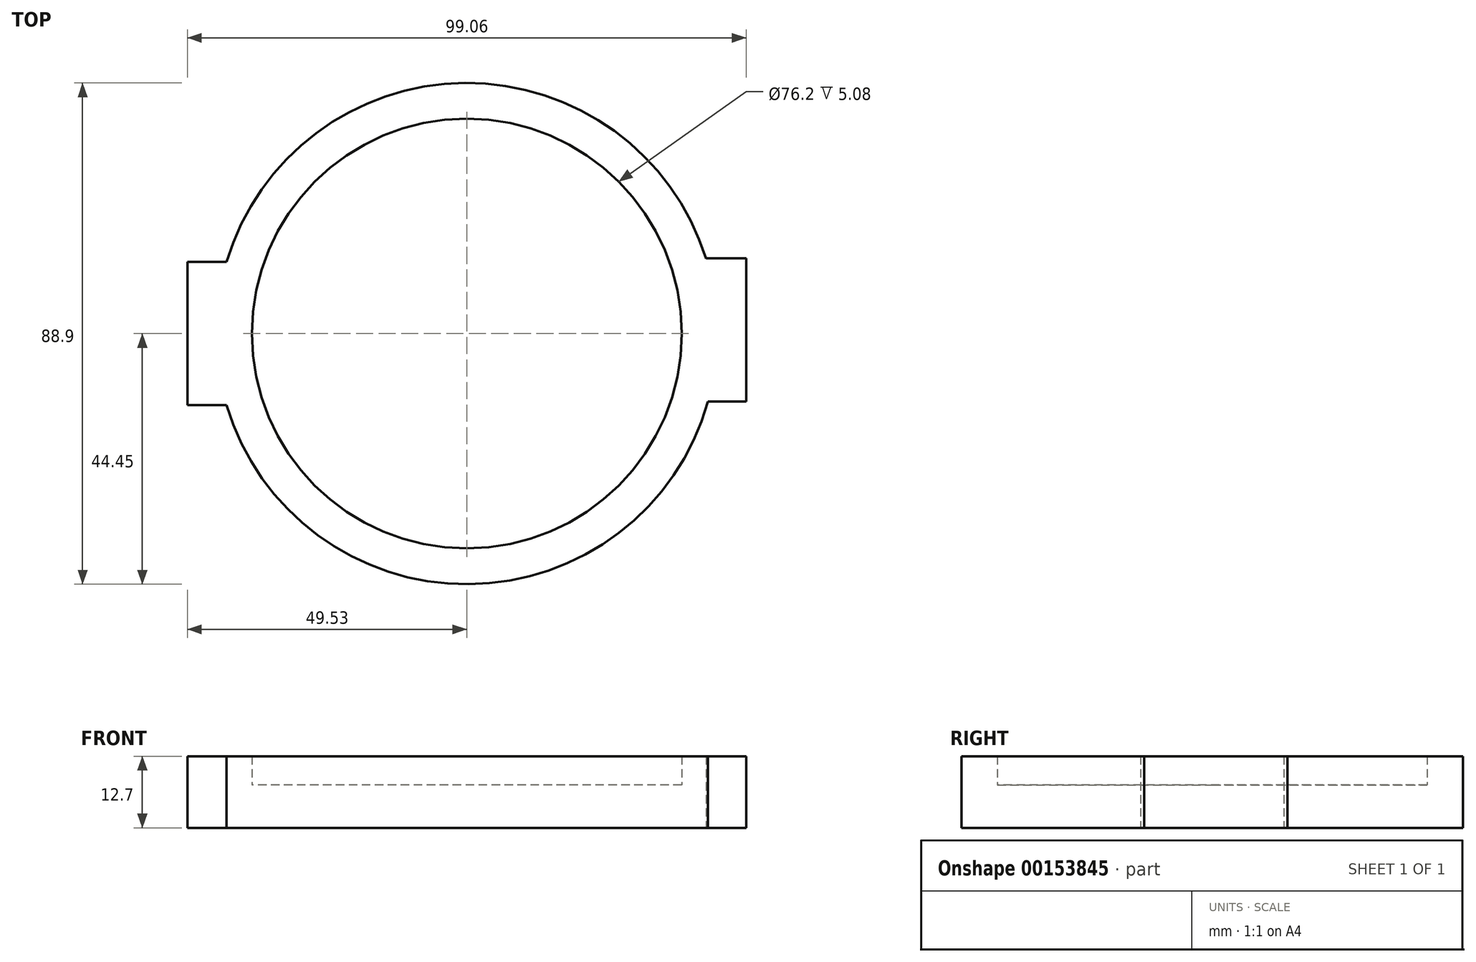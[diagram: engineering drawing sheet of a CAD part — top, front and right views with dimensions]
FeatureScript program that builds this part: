
annotation { "Feature Type Name" : "Feature", "Feature Type Description" : "" }
export const myFeature = defineFeature(function(context is Context, id is Id, definition is map)
    precondition{}
    {
        {
            var Q0;
            Q0=qCreatedBy(makeId("Top.planeOp"),FACE);
            var sketch = newSketch(context, id + "F0", { "sketchPlane" : qUnion([Q0])});
            skArc(sketch, "E0", {"start": v(-42.6, -12.7) * mm, "mid": v(0.32, -44.45) * mm, "end": v(42.78, -12.08) * mm});
            skCircle(sketch, "E1", {"center": v(0, 0) * mm, "radius": 38.1 * mm});
            skLineSegment(sketch, "E2", {"start": v(0, 0) * mm, "end": v(0, 44.45) * mm});
            skLineSegment(sketch, "E3", {"start": v(-49.53, 12.7) * mm, "end": v(-42.6, 12.7) * mm});
            skLineSegment(sketch, "E4", {"start": v(-49.53, -12.7) * mm, "end": v(-42.6, -12.7) * mm});
            skLineSegment(sketch, "E5", {"start": v(49.53, 13.32) * mm, "end": v(42.4, 13.32) * mm});
            skLineSegment(sketch, "E6", {"start": v(49.53, -12.08) * mm, "end": v(42.78, -12.08) * mm});
            skLineSegment(sketch, "E7", {"start": v(-49.53, 12.7) * mm, "end": v(-49.53, -12.7) * mm});
            skLineSegment(sketch, "E8", {"start": v(49.53, 13.32) * mm, "end": v(49.53, -12.08) * mm});
            skArc(sketch, "E9.trimOffspring", {"start": v(42.4, 13.32) * mm, "mid": v(-0.33, 44.45) * mm, "end": v(-42.6, 12.7) * mm});
            skLineSegment(sketch, "E10", {"start": v(0, 0) * mm, "end": v(44.45, 0) * mm});
            skLineSegment(sketch, "E11", {"start": v(0, 0) * mm, "end": v(-44.45, 0) * mm});
            skSolve(sketch);
        }
        {
            var Q0;
            Q0=makeQuery(id+"F0.imprint","IMPRINT",FACE,{"disambiguationData":[TD([[makeQuery(id+"F0.imprint","IMPRINT",EDGE,{"derivedFrom":sQuery(id+"F0.wireOp",EDGE,"E0")}),1.0]])]});
            extrude(context, id + "F1", {"entities" : qUnion([Q0]), "depth" : 12.7 * mm});
        }
        {
            var Q0;
            {var subQ0=sQuery(id+"F0.wireOp",EDGE,"E10");var subQ1=sQuery(id+"F0.wireOp",EDGE,"E1");var subQ2=makeQuery(id+"F0.imprint","INTERSECT",VERTEX,{"derivedFrom":[subQ1,subQ0]});Q0=makeQuery(id+"F0.imprint","IMPRINT",FACE,{"disambiguationData":[TD([[makeQuery(id+"F0.imprint","IMPRINT",EDGE,{"disambiguationData":[TD([[subQ2,1.0]])],"derivedFrom":subQ1}),1.0]])]});}
            var Q1;
            {var subQ0=sQuery(id+"F0.wireOp",EDGE,"E2");var subQ1=sQuery(id+"F0.wireOp",EDGE,"E1");var subQ2=makeQuery(id+"F0.imprint","INTERSECT",VERTEX,{"derivedFrom":[subQ1,subQ0]});Q1=makeQuery(id+"F0.imprint","IMPRINT",FACE,{"disambiguationData":[TD([[makeQuery(id+"F0.imprint","IMPRINT",EDGE,{"disambiguationData":[TD([[subQ2,-1.0]])],"derivedFrom":subQ1}),1.0]])]});}
            var Q2;
            {var subQ0=sQuery(id+"F0.wireOp",EDGE,"E2");var subQ1=sQuery(id+"F0.wireOp",EDGE,"E1");var subQ2=makeQuery(id+"F0.imprint","INTERSECT",VERTEX,{"derivedFrom":[subQ1,subQ0]});Q2=makeQuery(id+"F0.imprint","IMPRINT",FACE,{"disambiguationData":[TD([[makeQuery(id+"F0.imprint","IMPRINT",EDGE,{"disambiguationData":[TD([[subQ2,1.0]])],"derivedFrom":subQ1}),1.0]])]});}
            extrude(context, id + "F2", {"entities" : qUnion([Q0, Q1, Q2]), "operationType" : NewBodyOperationType.ADD, "depth" : 7.62 * mm});
        }
    });
